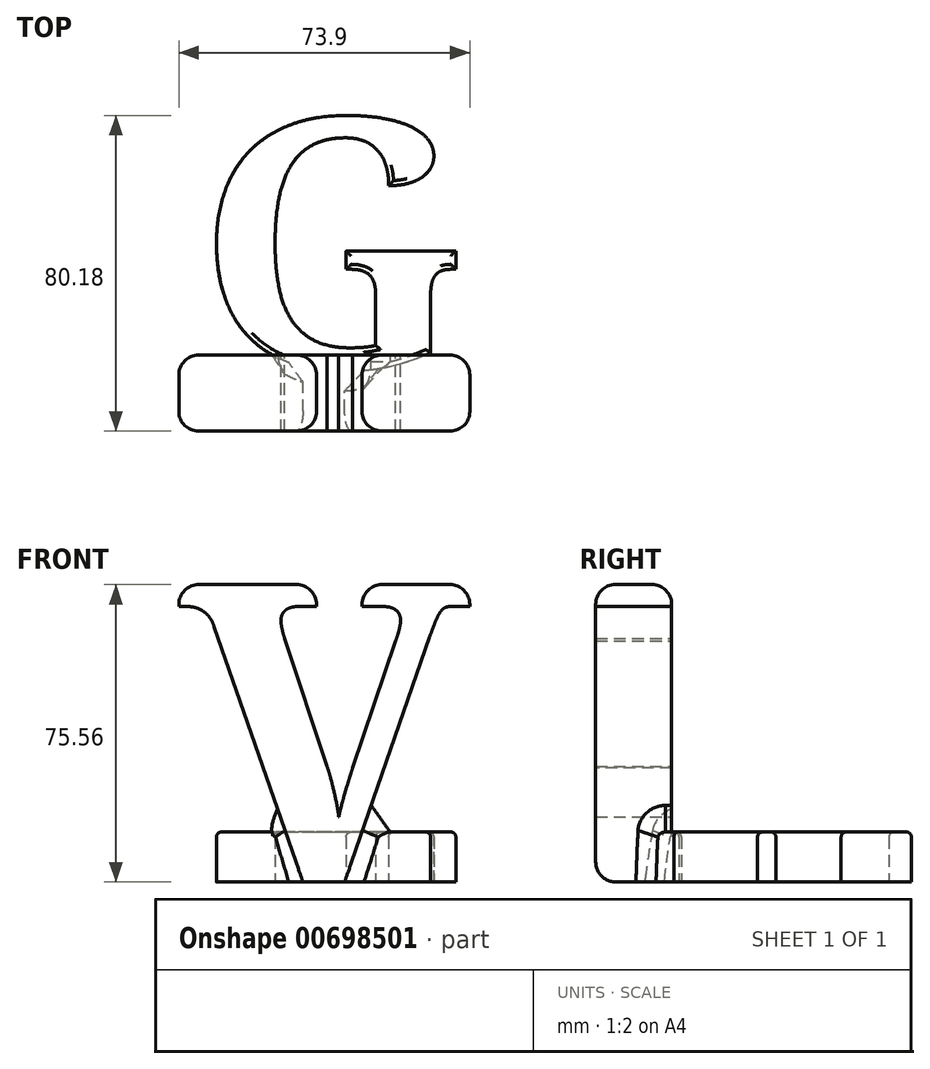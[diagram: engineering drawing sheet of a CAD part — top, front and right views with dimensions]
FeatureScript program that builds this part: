
annotation { "Feature Type Name" : "Feature", "Feature Type Description" : "" }
export const myFeature = defineFeature(function(context is Context, id is Id, definition is map)
    precondition{}
    {
        {
            var Q0;
            Q0=qCreatedBy(makeId("Top.planeOp"),FACE);
            var sketch = newSketch(context, id + "F0", { "sketchPlane" : qUnion([Q0])});
            skText(sketch, "E0", { "text": "G", "fontName": "NotoSerif-Bold.ttf"});
            const initialGuessF0  = {"E0": [-0.03572, -0.0319, 1, 0, 0.06382]};
            skSetInitialGuess(sketch, initialGuessF0);
            skSolve(sketch);
        }
        {
            var Q0;
            Q0 = qSketchRegion(id + "F0", true);
            extrude(context, id + "F1", {"entities" : qUnion([Q0]), "depth" : 12.7 * mm, "offsetDistance" : 25.4 * mm});
        }
        {
            var Q0;
            Q0=makeQuery(id+"F1.opExtrude","CAP_EDGE",EDGE,{"disambiguationData":[OSD([sQuery(id+"F0.wireOp",EDGE,"E0.sketch_text.stroke-0")])],"isStart":false});
            var Q1;
            Q1=makeQuery(id+"F1.opExtrude","CAP_EDGE",EDGE,{"disambiguationData":[OSD([sQuery(id+"F0.wireOp",EDGE,"E0.sketch_text.stroke-23")])],"isStart":false});
            var Q2;
            Q2=makeQuery(id+"F1.opExtrude","CAP_EDGE",EDGE,{"disambiguationData":[OSD([sQuery(id+"F0.wireOp",EDGE,"E0.sketch_text.stroke-30")])],"isStart":false});
            var Q3;
            Q3=makeQuery(id+"F1.opExtrude","CAP_EDGE",EDGE,{"disambiguationData":[OSD([sQuery(id+"F0.wireOp",EDGE,"E0.sketch_text.stroke-42")])],"isStart":false});
            var Q4;
            Q4=makeQuery(id+"F1.opExtrude","CAP_EDGE",EDGE,{"disambiguationData":[OSD([sQuery(id+"F0.wireOp",EDGE,"E0.sketch_text.stroke-35")])],"isStart":false});
            var Q5;
            Q5=makeQuery(id+"F1.opExtrude","CAP_EDGE",EDGE,{"disambiguationData":[OSD([sQuery(id+"F0.wireOp",EDGE,"E0.sketch_text.stroke-36")])],"isStart":false});
            var Q6;
            Q6=makeQuery(id+"F1.opExtrude","CAP_EDGE",EDGE,{"disambiguationData":[OSD([sQuery(id+"F0.wireOp",EDGE,"E0.sketch_text.stroke-34")])],"isStart":false});
            fillet(context, id + "F2", {"entities" : qUnion([Q0, Q1, Q2, Q3, Q4, Q5, Q6]), "radius" : 1.27 * mm, "tangentPropagation" : true, "allowEdgeOverflow" : false});
        }
        {
            var Q0;
            Q0=qCreatedBy(makeId("Front.planeOp"),FACE);
            cPlane(context, id + "F3", {"entities" : qUnion([Q0]), "cplaneType" : CPlaneType.OFFSET, "offset" : 31.9 * mm, "width" : 152.4 * mm, "height" : 152.4 * mm});
        }
        {
            var Q0;
            Q0=qCreatedBy(id+"F3.planeOp",FACE);
            var sketch = newSketch(context, id + "F4", { "sketchPlane" : qUnion([Q0])});
            skText(sketch, "E1", { "text": "V", "fontName": "NotoSerif-Bold.ttf"});
            const initialGuessF4  = {"E1": [-0.04038, 0, 1, 0, 0.0762]};
            skSetInitialGuess(sketch, initialGuessF4);
            skSolve(sketch);
        }
        {
            var Q0;
            Q0 = qSketchRegion(id + "F4", true);
            extrude(context, id + "F5", {"entities" : qUnion([Q0]), "operationType" : NewBodyOperationType.ADD, "endBound" : BoundingType.SYMMETRIC, "depth" : 6.6 * mm, "offsetDistance" : 25.4 * mm});
        }
        {
            var Q0;
            Q0=makeQuery(id+"F5.opExtrude","CAP_FACE",FACE,{"disambiguationData":[OSD([sQuery(id+"F4.wireOp",EDGE,"E1.sketch_text.stroke-0"),sQuery(id+"F4.wireOp",EDGE,"E1.sketch_text.stroke-1"),sQuery(id+"F4.wireOp",EDGE,"E1.sketch_text.stroke-2"),sQuery(id+"F4.wireOp",EDGE,"E1.sketch_text.stroke-3"),sQuery(id+"F4.wireOp",EDGE,"E1.sketch_text.stroke-4"),sQuery(id+"F4.wireOp",EDGE,"E1.sketch_text.stroke-5"),sQuery(id+"F4.wireOp",EDGE,"E1.sketch_text.stroke-6"),sQuery(id+"F4.wireOp",EDGE,"E1.sketch_text.stroke-7"),sQuery(id+"F4.wireOp",EDGE,"E1.sketch_text.stroke-8"),sQuery(id+"F4.wireOp",EDGE,"E1.sketch_text.stroke-9"),sQuery(id+"F4.wireOp",EDGE,"E1.sketch_text.stroke-10"),sQuery(id+"F4.wireOp",EDGE,"E1.sketch_text.stroke-11"),sQuery(id+"F4.wireOp",EDGE,"E1.sketch_text.stroke-12"),sQuery(id+"F4.wireOp",EDGE,"E1.sketch_text.stroke-13"),sQuery(id+"F4.wireOp",EDGE,"E1.sketch_text.stroke-14"),sQuery(id+"F4.wireOp",EDGE,"E1.sketch_text.stroke-15"),sQuery(id+"F4.wireOp",EDGE,"E1.sketch_text.stroke-16"),sQuery(id+"F4.wireOp",EDGE,"E1.sketch_text.stroke-17"),sQuery(id+"F4.wireOp",EDGE,"E1.sketch_text.stroke-18"),sQuery(id+"F4.wireOp",EDGE,"E1.sketch_text.stroke-19"),sQuery(id+"F4.wireOp",EDGE,"E1.sketch_text.stroke-20"),sQuery(id+"F4.wireOp",EDGE,"E1.sketch_text.stroke-21"),sQuery(id+"F4.wireOp",EDGE,"E1.sketch_text.stroke-22"),sQuery(id+"F4.wireOp",EDGE,"E1.sketch_text.stroke-23"),sQuery(id+"F4.wireOp",EDGE,"E1.sketch_text.stroke-24"),sQuery(id+"F4.wireOp",EDGE,"E1.sketch_text.stroke-25"),sQuery(id+"F4.wireOp",EDGE,"E1.sketch_text.stroke-26"),sQuery(id+"F4.wireOp",EDGE,"E1.sketch_text.stroke-27"),sQuery(id+"F4.wireOp",EDGE,"E1.sketch_text.stroke-28"),sQuery(id+"F4.wireOp",EDGE,"E1.sketch_text.stroke-29"),sQuery(id+"F4.wireOp",EDGE,"E1.sketch_text.stroke-30"),sQuery(id+"F4.wireOp",EDGE,"E1.sketch_text.stroke-31"),sQuery(id+"F4.wireOp",EDGE,"E1.sketch_text.stroke-32"),sQuery(id+"F4.wireOp",EDGE,"E1.sketch_text.stroke-33"),sQuery(id+"F4.wireOp",EDGE,"E1.sketch_text.stroke-34"),sQuery(id+"F4.wireOp",EDGE,"E1.sketch_text.stroke-35"),sQuery(id+"F4.wireOp",EDGE,"E1.sketch_text.stroke-36"),sQuery(id+"F4.wireOp",EDGE,"E1.sketch_text.stroke-37"),sQuery(id+"F4.wireOp",EDGE,"E1.sketch_text.stroke-38"),sQuery(id+"F4.wireOp",EDGE,"E1.sketch_text.stroke-39"),sQuery(id+"F4.wireOp",EDGE,"E1.sketch_text.stroke-40"),sQuery(id+"F4.wireOp",EDGE,"E1.sketch_text.stroke-41"),sQuery(id+"F4.wireOp",EDGE,"E1.sketch_text.stroke-42")])],"isStart":false});
            extrude(context, id + "F6", {"entities" : qUnion([Q0]), "operationType" : NewBodyOperationType.ADD, "depth" : 12.7 * mm, "offsetDistance" : 25.4 * mm});
        }
        {
            var Q0;
            {var subQ0=sQuery(id+"F4.wireOp",EDGE,"E1.sketch_text.stroke-14");var subQ1=sQuery(id+"F4.wireOp",EDGE,"E1.sketch_text.stroke-13");Q0=makeQuery(id+"F6.boolean.opBoolean","MERGE",EDGE,{"derivedFrom":[makeQuery(id+"F5.opExtrude","SWEPT_EDGE",EDGE,{"disambiguationData":[OSD([subQ1,subQ0])]}),makeQuery(id+"F6.opExtrude","SWEPT_EDGE",EDGE,{"disambiguationData":[OSD([subQ1,subQ0])]})]});}
            var Q1;
            {var subQ0=sQuery(id+"F4.wireOp",EDGE,"E1.sketch_text.stroke-15");var subQ1=sQuery(id+"F4.wireOp",EDGE,"E1.sketch_text.stroke-14");Q1=makeQuery(id+"F6.boolean.opBoolean","MERGE",EDGE,{"derivedFrom":[makeQuery(id+"F5.opExtrude","SWEPT_EDGE",EDGE,{"disambiguationData":[OSD([subQ1,subQ0])]}),makeQuery(id+"F6.opExtrude","SWEPT_EDGE",EDGE,{"disambiguationData":[OSD([subQ1,subQ0])]})]});}
            var Q2;
            {var subQ0=sQuery(id+"F4.wireOp",EDGE,"E1.sketch_text.stroke-41");var subQ1=sQuery(id+"F4.wireOp",EDGE,"E1.sketch_text.stroke-40");Q2=makeQuery(id+"F6.boolean.opBoolean","MERGE",EDGE,{"derivedFrom":[makeQuery(id+"F5.opExtrude","SWEPT_EDGE",EDGE,{"disambiguationData":[OSD([subQ1,subQ0])]}),makeQuery(id+"F6.opExtrude","SWEPT_EDGE",EDGE,{"disambiguationData":[OSD([subQ1,subQ0])]})]});}
            var Q3;
            {var subQ0=sQuery(id+"F4.wireOp",EDGE,"E1.sketch_text.stroke-42");var subQ1=sQuery(id+"F4.wireOp",EDGE,"E1.sketch_text.stroke-41");Q3=makeQuery(id+"F6.boolean.opBoolean","MERGE",EDGE,{"derivedFrom":[makeQuery(id+"F5.opExtrude","SWEPT_EDGE",EDGE,{"disambiguationData":[OSD([subQ1,subQ0])]}),makeQuery(id+"F6.opExtrude","SWEPT_EDGE",EDGE,{"disambiguationData":[OSD([subQ1,subQ0])]})]});}
            var Q4;
            Q4=makeQuery(id+"F6.opExtrude","CAP_EDGE",EDGE,{"disambiguationData":[OSD([sQuery(id+"F4.wireOp",EDGE,"E1.sketch_text.stroke-6")])],"isStart":false});
            fillet(context, id + "F7", {"entities" : qUnion([Q0, Q1, Q2, Q3, Q4]), "radius" : 5.08 * mm, "tangentPropagation" : true, "allowEdgeOverflow" : false});
        }
        {
            var Q0;
            Q0=makeQuery(id+"F5.boolean.opBoolean","INTERSECT",EDGE,{"derivedFrom":[makeQuery(id+"F1.opExtrude","SWEPT_FACE",FACE,{"disambiguationData":[OSD([sQuery(id+"F0.wireOp",EDGE,"E0.sketch_text.stroke-0")])]}),makeQuery(id+"F5.opExtrude","SWEPT_FACE",FACE,{"disambiguationData":[OSD([sQuery(id+"F4.wireOp",EDGE,"E1.sketch_text.stroke-7")])]})]});
            var Q1;
            Q1=makeQuery(id+"F5.boolean.opBoolean","INTERSECT",EDGE,{"derivedFrom":[makeQuery(id+"F1.opExtrude","SWEPT_FACE",FACE,{"disambiguationData":[OSD([sQuery(id+"F0.wireOp",EDGE,"E0.sketch_text.stroke-44")])]}),makeQuery(id+"F5.opExtrude","SWEPT_FACE",FACE,{"disambiguationData":[OSD([sQuery(id+"F4.wireOp",EDGE,"E1.sketch_text.stroke-5")])]})]});
            chamfer(context, id + "F8", {"entities" : qUnion([Q0, Q1]), "width" : 5.08 * mm, "tangentPropagation" : true});
        }
        {
            var Q0;
            Q0=makeQuery(id+"F6.opExtrude","CAP_EDGE",EDGE,{"disambiguationData":[OSD([sQuery(id+"F4.wireOp",EDGE,"E1.sketch_text.stroke-14")])],"isStart":false});
            var Q1;
            Q1=makeQuery(id+"F6.opExtrude","CAP_EDGE",EDGE,{"disambiguationData":[OSD([sQuery(id+"F4.wireOp",EDGE,"E1.sketch_text.stroke-41")])],"isStart":false});
            var Q2;
            Q2=makeQuery(id+"F5.opExtrude","CAP_EDGE",EDGE,{"disambiguationData":[OSD([sQuery(id+"F4.wireOp",EDGE,"E1.sketch_text.stroke-41")])],"isStart":true});
            var Q3;
            Q3=makeQuery(id+"F5.opExtrude","CAP_EDGE",EDGE,{"disambiguationData":[OSD([sQuery(id+"F4.wireOp",EDGE,"E1.sketch_text.stroke-14")])],"isStart":true});
            fillet(context, id + "F9", {"entities" : qUnion([Q0, Q1, Q2, Q3]), "radius" : 5 * mm, "tangentPropagation" : true, "allowEdgeOverflow" : false});
        }
    });
